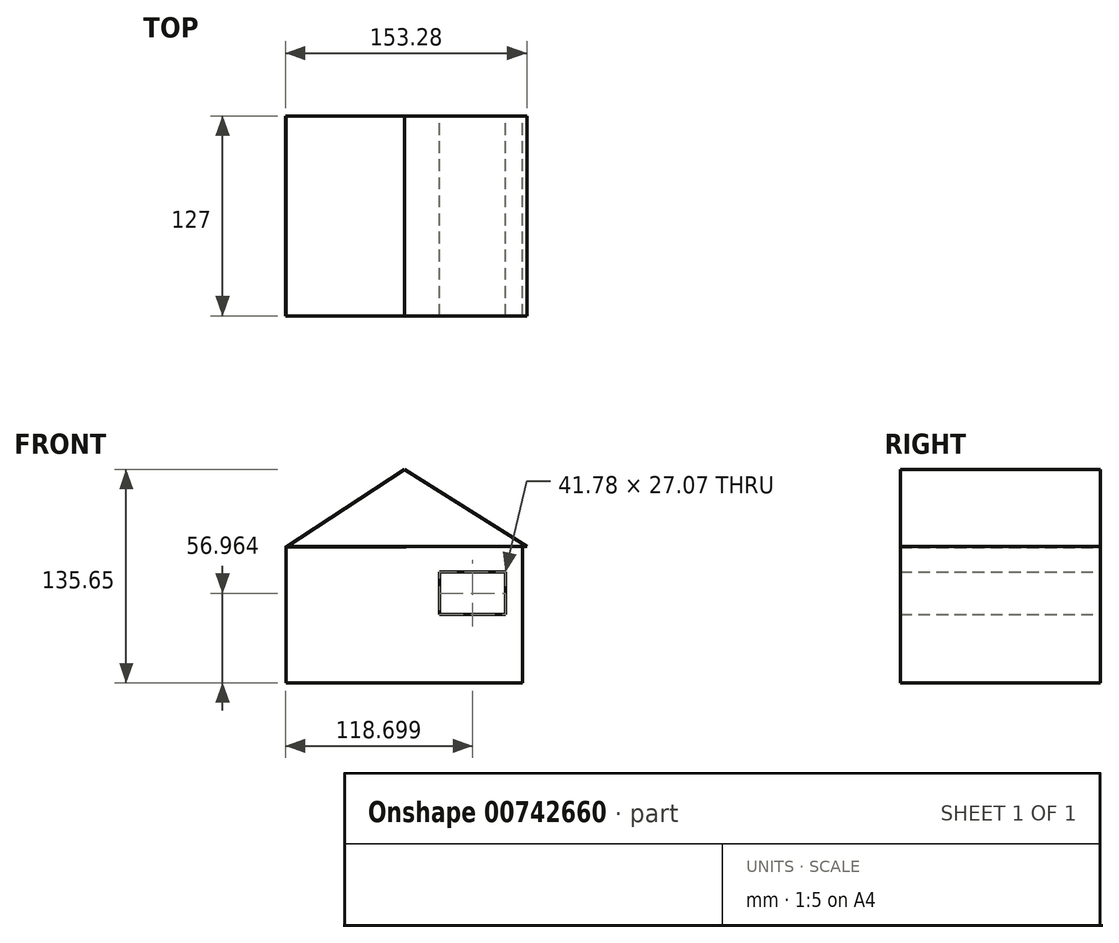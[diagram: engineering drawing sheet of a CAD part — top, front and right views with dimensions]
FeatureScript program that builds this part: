
annotation { "Feature Type Name" : "Feature", "Feature Type Description" : "" }
export const myFeature = defineFeature(function(context is Context, id is Id, definition is map)
    precondition{}
    {
        {
            var Q0;
            Q0=qCreatedBy(makeId("Front.planeOp"),FACE);
            var sketch = newSketch(context, id + "F0", { "sketchPlane" : qUnion([Q0])});
            skLineSegment(sketch, "E0.bottom", {"start": v(-75.1, -43.43) * mm, "end": v(75.1, -43.43) * mm});
            skLineSegment(sketch, "E0.top", {"start": v(-75.1, 43.43) * mm, "end": v(75.1, 43.43) * mm});
            skLineSegment(sketch, "E0.left", {"start": v(-75.1, -43.43) * mm, "end": v(-75.1, 43.43) * mm});
            skLineSegment(sketch, "E0.right", {"start": v(75.1, -43.43) * mm, "end": v(75.1, 43.43) * mm});
            skPoint(sketch, "E0.middle", {"position": v(0, 0) * mm});
            skSolve(sketch);
        }
        {
            var Q0;
            Q0=qCreatedBy(makeId("Front.planeOp"),FACE);
            var sketch = newSketch(context, id + "F1", { "sketchPlane" : qUnion([Q0])});
            skLineSegment(sketch, "E1", {"start": v(-75.44, 42.73) * mm, "end": v(0, 92.22) * mm});
            skLineSegment(sketch, "E2", {"start": v(0, 92.22) * mm, "end": v(77.84, 43.15) * mm});
            skLineSegment(sketch, "E3", {"start": v(77.84, 43.15) * mm, "end": v(-75.44, 42.73) * mm});
            skSolve(sketch);
        }
        {
            var Q0;
            Q0=makeQuery(id+"F0.imprint","IMPRINT",FACE,{"disambiguationData":[TD([[makeQuery(id+"F0.imprint","IMPRINT",EDGE,{"derivedFrom":sQuery(id+"F0.wireOp",EDGE,"E0.bottom")}),1.0]])]});
            var sketch = newSketch(context, id + "F2", { "sketchPlane" : qUnion([Q0])});
            skLineSegment(sketch, "E4.bottom", {"start": v(64.15, 27.07) * mm, "end": v(22.37, 27.07) * mm});
            skLineSegment(sketch, "E4.top", {"start": v(64.15, 0) * mm, "end": v(22.37, 0) * mm});
            skLineSegment(sketch, "E4.left", {"start": v(64.15, 27.07) * mm, "end": v(64.15, 0) * mm});
            skLineSegment(sketch, "E4.right", {"start": v(22.37, 27.07) * mm, "end": v(22.37, 0) * mm});
            skSolve(sketch);
        }
        {
            var Q0;
            Q0=makeQuery(id+"F2.imprint","IMPRINT",FACE,{"disambiguationData":[TD([[makeQuery(id+"F2.imprint","IMPRINT",EDGE,{"derivedFrom":sQuery(id+"F2.wireOp",EDGE,"E4.bottom")}),-1.0]])]});
            var sketch = newSketch(context, id + "F3", { "sketchPlane" : qUnion([Q0])});
            skLineSegment(sketch, "E5", {"start": v(-58.85, -44.03) * mm, "end": v(-58.85, 0) * mm});
            skLineSegment(sketch, "E6", {"start": v(-58.85, 0) * mm, "end": v(-27.62, 0) * mm});
            skLineSegment(sketch, "E7", {"start": v(-27.62, 0) * mm, "end": v(-27.62, -43.16) * mm});
            skSolve(sketch);
        }
        {
            var Q0;
            Q0=makeQuery(id+"F1.imprint","IMPRINT",FACE,{"disambiguationData":[TD([[makeQuery(id+"F1.imprint","IMPRINT",EDGE,{"derivedFrom":sQuery(id+"F1.wireOp",EDGE,"E1")}),-1.0]])]});
            var Q1;
            Q1=makeQuery(id+"F2.imprint","IMPRINT",FACE,{"disambiguationData":[TD([[makeQuery(id+"F2.imprint","IMPRINT",EDGE,{"derivedFrom":sQuery(id+"F2.wireOp",EDGE,"E4.bottom")}),-1.0]])]});
            extrude(context, id + "F4", {"entities" : qUnion([Q0, Q1]), "depth" : 127 * mm, "offsetDistance" : 25.4 * mm});
        }
    });
